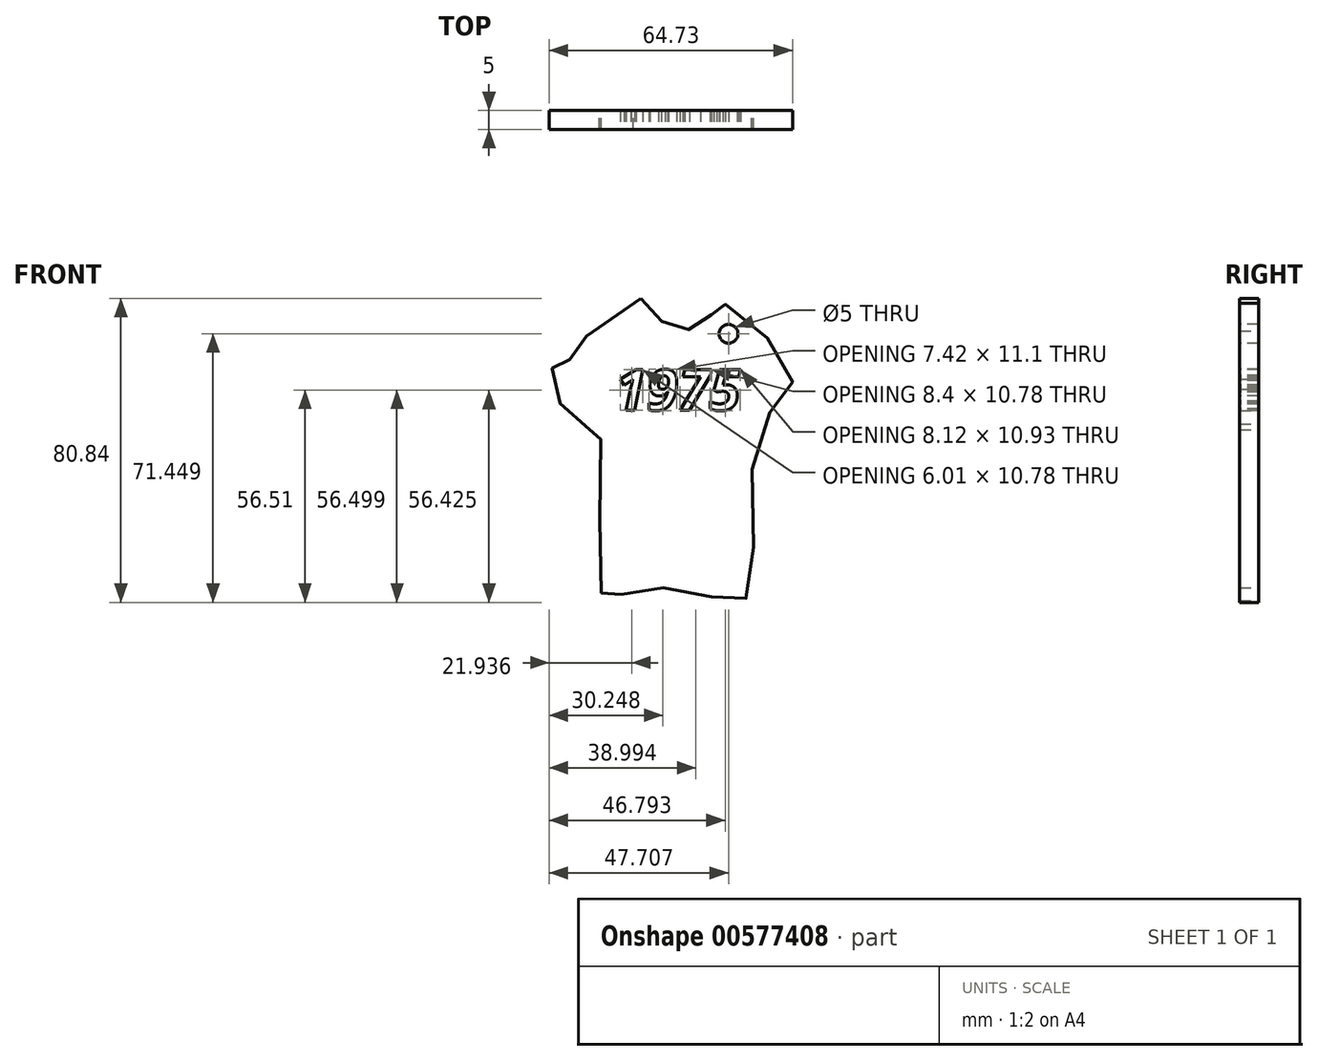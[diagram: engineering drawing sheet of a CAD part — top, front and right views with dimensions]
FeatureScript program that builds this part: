
annotation { "Feature Type Name" : "Feature", "Feature Type Description" : "" }
export const myFeature = defineFeature(function(context is Context, id is Id, definition is map)
    precondition{}
    {
        {
            var Q0;
            Q0=qCreatedBy(makeId("Front.planeOp"),FACE);
            var sketch = newSketch(context, id + "F0", { "sketchPlane" : qUnion([Q0])});
            skPoint(sketch, "E0.16.internal.snap0", {"position": v(-33.41, -42.38) * mm});
            skFitSpline(sketch, "E0", {"points": [v(-40.22, 40.38) * mm, v(-47.67, 35.09) * mm, v(-57.87, 27.43) * mm, v(-60.62, 22.33) * mm, v(-64.54, 21.2) * mm, v(-55.13, 5.47) * mm, v(-51.6, 6.88) * mm, v(-50.42, -39.08) * mm, v(-46.1, -38.62) * mm, v(-26.1, -37.55) * mm, v(-11.97, -38.96) * mm, v(-8.83, 5.5) * mm, v(0, 19.7) * mm, v(-18.64, 39.15) * mm, v(-20.6, 37.4) * mm, v(-25.7, 32.8) * mm, v(-33.41, 33.11) * mm, v(-40.22, 40.38) * mm]});
            skSolve(sketch);
        }
        {
            var Q0;
            Q0=makeQuery(id+"F0.imprint","IMPRINT",FACE,{"disambiguationData":[TD([[makeQuery(id+"F0.imprint","IMPRINT",EDGE,{"derivedFrom":sQuery(id+"F0.wireOp",EDGE,"E0")}),1.0]])]});
            extrude(context, id + "F1", {"entities" : qUnion([Q0]), "depth" : 5 * mm, "offsetDistance" : 25 * mm});
        }
        {
            var Q0;
            Q0=makeQuery(id+"F1.opExtrude","CAP_FACE",FACE,{"disambiguationData":[OSD([sQuery(id+"F0.wireOp",EDGE,"E0")])],"isStart":false});
            var sketch = newSketch(context, id + "F2", { "sketchPlane" : qUnion([Q0])});
            skText(sketch, "E1", { "text": "1975\n", "fontName": "OpenSans-BoldItalic.ttf"});
            const initialGuessF2  = {"E1": [-0.04706, 0.0107, 1, 0, 0.01087]};
            skSetInitialGuess(sketch, initialGuessF2);
            skSolve(sketch);
        }
        {
            var Q0;
            Q0=makeQuery(id+"F1.opExtrude","CAP_FACE",FACE,{"disambiguationData":[OSD([sQuery(id+"F0.wireOp",EDGE,"E0")])],"isStart":false});
            var sketch = newSketch(context, id + "F3", { "sketchPlane" : qUnion([Q0])});
            skPoint(sketch, "E2", {"position": v(-16.94, 31.04) * mm});
            skSolve(sketch);
        }
        {
            var Q0;
            Q0=sQuery(id+"F3.wireOp",VERTEX,"E2");
            var Q1;
            Q1=makeQuery(id+"F1.opExtrude","SWEPT_BODY",BODY,{"disambiguationData":[OSD([sQuery(id+"F0.wireOp",EDGE,"E0")])]});
            hole(context, id + "F4", {"style" : HoleStyle.SIMPLE, "endStyle" : HoleEndStyle.THROUGH, "holeDiameter" : 5 * mm, "majorDiameter" : 5 * mm, "isTappedThrough" : true, "tappedDepth" : 12 * mm, "tapClearance" : 3, "locations" : qUnion([Q0]), "scope" : qUnion([Q1])});
        }
        {
            var Q0;
            Q0 = qSketchRegion(id + "F2", true);
            extrude(context, id + "F5", {"entities" : qUnion([Q0]), "operationType" : NewBodyOperationType.REMOVE, "oppositeDirection" : true, "depth" : 25 * mm, "offsetDistance" : 25 * mm});
        }
    });
